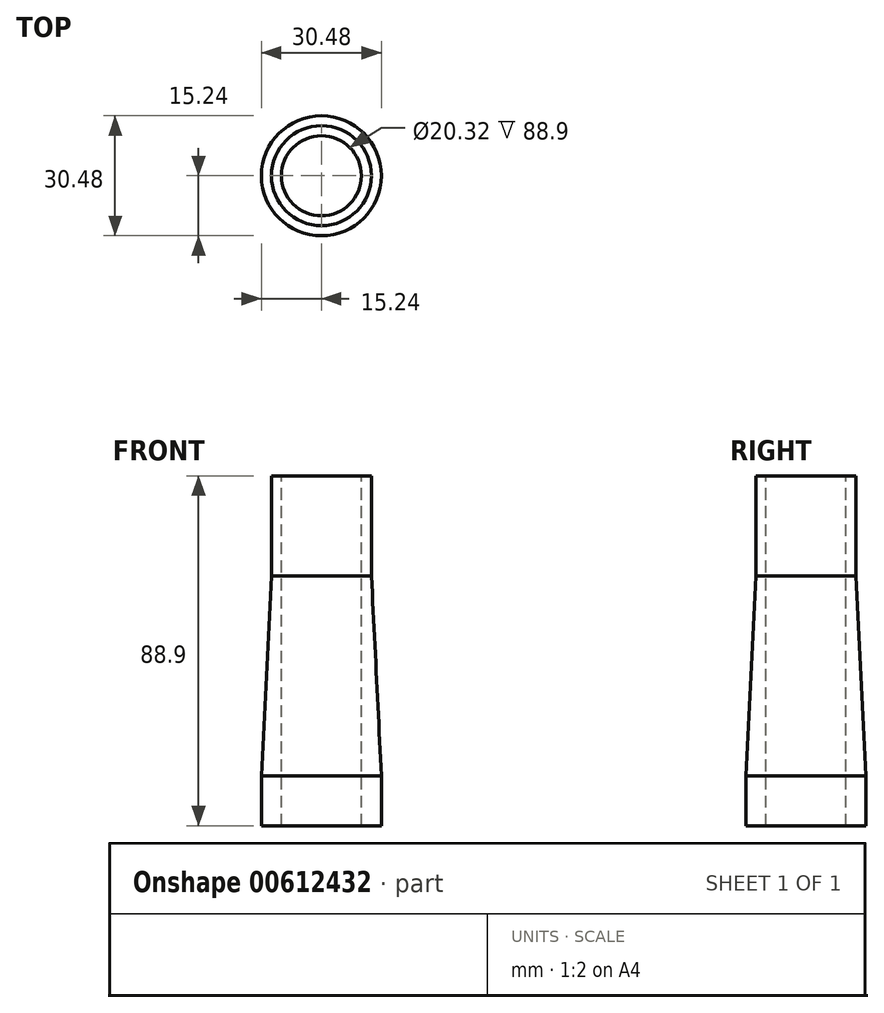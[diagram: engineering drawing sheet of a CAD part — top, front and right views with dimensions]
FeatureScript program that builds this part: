
annotation { "Feature Type Name" : "Feature", "Feature Type Description" : "" }
export const myFeature = defineFeature(function(context is Context, id is Id, definition is map)
    precondition{}
    {
        {
            var Q0;
            Q0=qCreatedBy(makeId("Top.planeOp"),FACE);
            var sketch = newSketch(context, id + "F0", { "sketchPlane" : qUnion([Q0])});
            skCircle(sketch, "E0", {"center": v(0, 0) * mm, "radius": 15.24 * mm});
            skSolve(sketch);
        }
        {
            var Q0;
            Q0 = qSketchRegion(id + "F0", true);
            extrude(context, id + "F1", {"entities" : qUnion([Q0]), "depth" : 12.7 * mm, "offsetDistance" : 25.4 * mm});
        }
        {
            var Q0;
            Q0=makeQuery(id+"F1.opExtrude","CAP_FACE",FACE,{"disambiguationData":[OSD([sQuery(id+"F0.wireOp",EDGE,"E0")])],"isStart":false});
            cPlane(context, id + "F2", {"entities" : qUnion([Q0]), "cplaneType" : CPlaneType.OFFSET, "offset" : 50.8 * mm, "width" : 152.4 * mm, "height" : 152.4 * mm});
        }
        {
            var Q0;
            Q0=qCreatedBy(id+"F2.planeOp",FACE);
            var sketch = newSketch(context, id + "F3", { "sketchPlane" : qUnion([Q0])});
            skCircle(sketch, "E1", {"center": v(0, 0) * mm, "radius": 12.7 * mm});
            skSolve(sketch);
        }
        {
            var Q1;
            Q1 = qSketchRegion(id + "F3", true);
            var Q2;
            Q2=makeQuery(id+"F1.opExtrude","CAP_FACE",FACE,{"disambiguationData":[OSD([sQuery(id+"F0.wireOp",EDGE,"E0")])],"isStart":false});
            loft(context, id + "F4", {"operationType" : NewBodyOperationType.ADD, "sheetProfilesArray" : [{ "sheetProfileEntities" : qUnion([Q1]) }, { "sheetProfileEntities" : qUnion([Q2]) }]});
        }
        {
            var Q0;
            Q0=makeQuery(id+"F4.opLoft","CAP_FACE",FACE,{"disambiguationData":[OSD([makeQuery(id+"F3.imprint","IMPRINT",FACE,{"disambiguationData":[TD([[makeQuery(id+"F3.imprint","IMPRINT",EDGE,{"derivedFrom":sQuery(id+"F3.wireOp",EDGE,"E1")}),1.0]])]})])],"isStart":true});
            var sketch = newSketch(context, id + "F5", { "sketchPlane" : qUnion([Q0])});
            skCircle(sketch, "E2.0", {"center": v(0, 0) * mm, "radius": 12.7 * mm});
            skSolve(sketch);
        }
        {
            var Q0;
            Q0 = qSketchRegion(id + "F5", true);
            extrude(context, id + "F6", {"entities" : qUnion([Q0]), "operationType" : NewBodyOperationType.ADD, "depth" : 25.4 * mm, "offsetDistance" : 25.4 * mm});
        }
        {
            var Q0;
            Q0=makeQuery(id+"F6.opExtrude","CAP_FACE",FACE,{"disambiguationData":[OSD([sQuery(id+"F5.wireOp",EDGE,"E2.0")])],"isStart":false});
            var sketch = newSketch(context, id + "F7", { "sketchPlane" : qUnion([Q0])});
            skCircle(sketch, "E3", {"center": v(0, 0) * mm, "radius": 10.16 * mm});
            skSolve(sketch);
        }
        {
            var Q0;
            Q0 = qSketchRegion(id + "F7", true);
            extrude(context, id + "F8", {"entities" : qUnion([Q0]), "operationType" : NewBodyOperationType.REMOVE, "endBound" : BoundingType.THROUGH_ALL, "oppositeDirection" : true, "depth" : 25.4 * mm, "offsetDistance" : 25.4 * mm});
        }
    });
